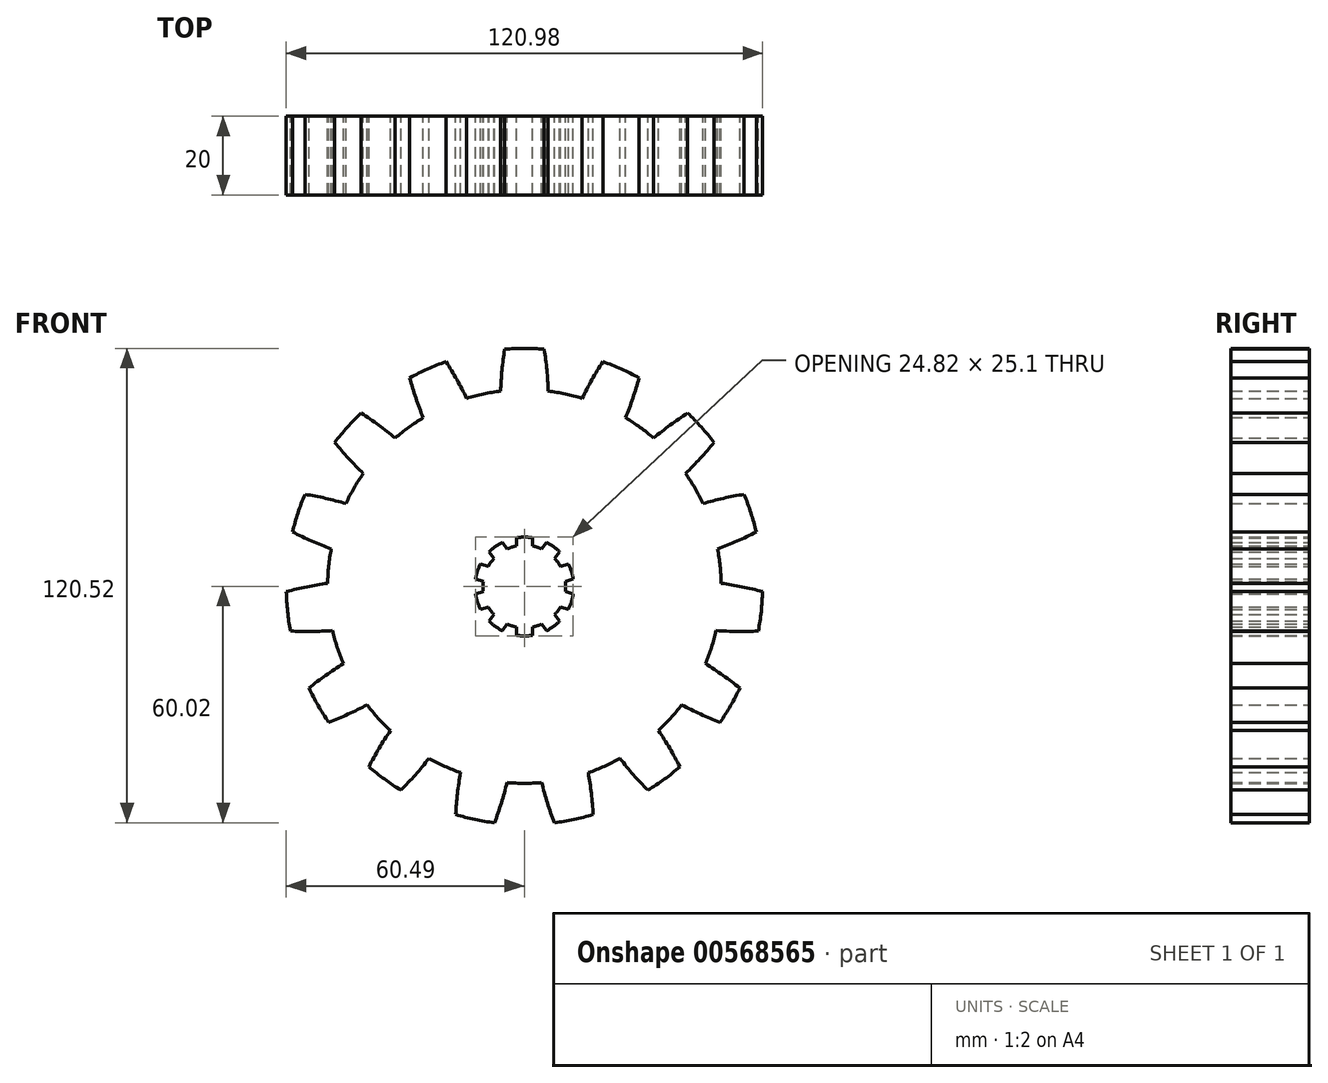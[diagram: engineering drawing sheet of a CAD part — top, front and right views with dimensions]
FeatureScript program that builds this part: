
annotation { "Feature Type Name" : "Feature", "Feature Type Description" : "" }
export const myFeature = defineFeature(function(context is Context, id is Id, definition is map)
    precondition{}
    {
        {
            var Q0;
            Q0=qCreatedBy(makeId("Front.planeOp"),FACE);
            var sketch = newSketch(context, id + "F0", { "sketchPlane" : qUnion([Q0])});
            skCircle(sketch, "E0", {"center": v(0, 0) * mm, "radius": 50 * mm});
            skLineSegment(sketch, "E1", {"start": v(-16.39, 46.5) * mm, "end": v(83.9, 46.5) * mm, "construction": true});
            skLineSegment(sketch, "E2", {"start": v(83.9, 46.5) * mm, "end": v(83.9, 27.65) * mm, "construction": true});
            skLineSegment(sketch, "E3", {"start": v(83.9, 46.5) * mm, "end": v(83.9, 51.66) * mm, "construction": true});
            skLineSegment(sketch, "E4", {"start": v(0, -2.7) * mm, "end": v(0, 89.14) * mm, "construction": true});
            skLineSegment(sketch, "E5", {"start": v(0, 50) * mm, "end": v(-34.34, 50) * mm, "construction": true});
            skArc(sketch, "E6", {"start": v(-5.04, 60.29) * mm, "mid": v(-5.7, 54.98) * mm, "end": v(-6.05, 49.63) * mm});
            skArc(sketch, "E7.MirrorCS", {"start": v(5.04, 60.29) * mm, "mid": v(5.7, 54.98) * mm, "end": v(6.05, 49.63) * mm});
            skArc(sketch, "E8.trimOffspring", {"start": v(5.04, 60.29) * mm, "mid": v(0, 60.5) * mm, "end": v(-5.04, 60.29) * mm});
            skArc(sketch, "E9.1.0", {"start": v(-19.92, 57.13) * mm, "mid": v(-24.6, 55.27) * mm, "end": v(-29.12, 53.03) * mm});
            skArc(sketch, "E9.2.0", {"start": v(-41.43, 44.09) * mm, "mid": v(-44.96, 40.48) * mm, "end": v(-48.17, 36.6) * mm});
            skArc(sketch, "E10.3.3.0", {"start": v(-55.78, 23.42) * mm, "mid": v(-57.54, 18.7) * mm, "end": v(-58.9, 13.84) * mm});
            skArc(sketch, "E10.3.4.0", {"start": v(-60.49, -1.3) * mm, "mid": v(-60.17, -6.32) * mm, "end": v(-59.43, -11.31) * mm});
            skArc(sketch, "E10.3.5.0", {"start": v(-54.73, -25.78) * mm, "mid": v(-52.4, -30.25) * mm, "end": v(-49.7, -34.5) * mm});
            skArc(sketch, "E10.3.6.0", {"start": v(-39.51, -45.81) * mm, "mid": v(-35.56, -48.95) * mm, "end": v(-31.36, -51.74) * mm});
            skArc(sketch, "E10.3.7.0", {"start": v(-17.46, -57.93) * mm, "mid": v(-12.58, -59.18) * mm, "end": v(-7.6, -60.02) * mm});
            skArc(sketch, "E10.3.8.0", {"start": v(7.6, -60.02) * mm, "mid": v(12.58, -59.18) * mm, "end": v(17.46, -57.93) * mm});
            skArc(sketch, "E10.3.9.0", {"start": v(31.36, -51.74) * mm, "mid": v(35.56, -48.95) * mm, "end": v(39.51, -45.81) * mm});
            skArc(sketch, "E10.3.10.0", {"start": v(49.7, -34.5) * mm, "mid": v(52.4, -30.25) * mm, "end": v(54.73, -25.78) * mm});
            skArc(sketch, "E10.3.11.0", {"start": v(59.43, -11.31) * mm, "mid": v(60.17, -6.32) * mm, "end": v(60.49, -1.3) * mm});
            skArc(sketch, "E10.3.12.0", {"start": v(58.9, 13.84) * mm, "mid": v(57.54, 18.7) * mm, "end": v(55.78, 23.42) * mm});
            skArc(sketch, "E10.3.13.0", {"start": v(48.17, 36.6) * mm, "mid": v(44.96, 40.48) * mm, "end": v(41.43, 44.09) * mm});
            skArc(sketch, "E10.3.14.0", {"start": v(29.12, 53.03) * mm, "mid": v(24.6, 55.27) * mm, "end": v(19.92, 57.13) * mm});
            skArc(sketch, "E11.1.0", {"start": v(-29.12, 53.03) * mm, "mid": v(-27.57, 47.9) * mm, "end": v(-25.71, 42.88) * mm});
            skArc(sketch, "E11.1.2", {"start": v(-19.92, 57.13) * mm, "mid": v(-17.15, 52.54) * mm, "end": v(-14.66, 47.8) * mm});
            skArc(sketch, "E11.2.0", {"start": v(-48.17, 36.6) * mm, "mid": v(-44.67, 32.55) * mm, "end": v(-40.93, 28.72) * mm});
            skArc(sketch, "E11.2.2", {"start": v(-41.43, 44.09) * mm, "mid": v(-37.04, 41.02) * mm, "end": v(-32.84, 37.7) * mm});
            skArc(sketch, "E11.3.0", {"start": v(-58.9, 13.84) * mm, "mid": v(-54.05, 11.57) * mm, "end": v(-49.07, 9.59) * mm});
            skArc(sketch, "E11.3.2", {"start": v(-55.78, 23.42) * mm, "mid": v(-50.52, 22.4) * mm, "end": v(-45.34, 21.09) * mm});
            skArc(sketch, "E11.4.0", {"start": v(-59.43, -11.31) * mm, "mid": v(-54.08, -11.42) * mm, "end": v(-48.73, -11.2) * mm});
            skArc(sketch, "E11.4.2", {"start": v(-60.49, -1.3) * mm, "mid": v(-55.27, -0.08) * mm, "end": v(-50, 0.82) * mm});
            skArc(sketch, "E11.5.0", {"start": v(-49.7, -34.5) * mm, "mid": v(-44.76, -32.42) * mm, "end": v(-39.96, -30.05) * mm});
            skArc(sketch, "E11.5.2", {"start": v(-54.73, -25.78) * mm, "mid": v(-50.46, -22.55) * mm, "end": v(-46, -19.58) * mm});
            skArc(sketch, "E11.6.0", {"start": v(-31.36, -51.74) * mm, "mid": v(-27.7, -47.83) * mm, "end": v(-24.28, -43.7) * mm});
            skArc(sketch, "E11.6.2", {"start": v(-39.51, -45.81) * mm, "mid": v(-36.93, -41.13) * mm, "end": v(-34.06, -36.6) * mm});
            skArc(sketch, "E11.7.0", {"start": v(-7.6, -60.02) * mm, "mid": v(-5.85, -54.96) * mm, "end": v(-4.4, -49.8) * mm});
            skArc(sketch, "E11.7.2", {"start": v(-17.46, -57.93) * mm, "mid": v(-17, -52.6) * mm, "end": v(-16.23, -47.3) * mm});
            skArc(sketch, "E11.8.0", {"start": v(17.46, -57.93) * mm, "mid": v(17, -52.6) * mm, "end": v(16.23, -47.3) * mm});
            skArc(sketch, "E11.8.2", {"start": v(7.6, -60.02) * mm, "mid": v(5.85, -54.96) * mm, "end": v(4.4, -49.8) * mm});
            skArc(sketch, "E11.9.0", {"start": v(39.51, -45.81) * mm, "mid": v(36.93, -41.13) * mm, "end": v(34.06, -36.6) * mm});
            skArc(sketch, "E11.9.2", {"start": v(31.36, -51.74) * mm, "mid": v(27.7, -47.83) * mm, "end": v(24.28, -43.7) * mm});
            skArc(sketch, "E11.10.0", {"start": v(54.73, -25.78) * mm, "mid": v(50.46, -22.55) * mm, "end": v(46, -19.58) * mm});
            skArc(sketch, "E11.10.2", {"start": v(49.7, -34.5) * mm, "mid": v(44.76, -32.42) * mm, "end": v(39.96, -30.05) * mm});
            skArc(sketch, "E11.11.0", {"start": v(60.49, -1.3) * mm, "mid": v(55.27, -0.08) * mm, "end": v(50, 0.82) * mm});
            skArc(sketch, "E11.11.2", {"start": v(59.43, -11.31) * mm, "mid": v(54.08, -11.42) * mm, "end": v(48.73, -11.2) * mm});
            skArc(sketch, "E11.12.0", {"start": v(55.78, 23.42) * mm, "mid": v(50.52, 22.4) * mm, "end": v(45.34, 21.09) * mm});
            skArc(sketch, "E11.12.2", {"start": v(58.9, 13.84) * mm, "mid": v(54.05, 11.57) * mm, "end": v(49.07, 9.59) * mm});
            skArc(sketch, "E11.13.0", {"start": v(41.43, 44.09) * mm, "mid": v(37.04, 41.02) * mm, "end": v(32.84, 37.7) * mm});
            skArc(sketch, "E11.13.2", {"start": v(48.17, 36.6) * mm, "mid": v(44.67, 32.55) * mm, "end": v(40.93, 28.72) * mm});
            skArc(sketch, "E11.14.0", {"start": v(19.92, 57.13) * mm, "mid": v(17.15, 52.54) * mm, "end": v(14.66, 47.8) * mm});
            skArc(sketch, "E11.14.2", {"start": v(29.12, 53.03) * mm, "mid": v(27.57, 47.9) * mm, "end": v(25.71, 42.88) * mm});
            skSolve(sketch);
        }
        {
            var Q0;
            {var subQ0=sQuery(id+"F0.wireOp",EDGE,"E0");var subQ18=makeQuery(id+"F0.imprint","INTERSECT",VERTEX,{"derivedFrom":[subQ0,sQuery(id+"F0.wireOp",EDGE,"E11.11.0")]});Q0=makeQuery(id+"F0.imprint","IMPRINT",FACE,{"disambiguationData":[TD([[makeQuery(id+"F0.imprint","IMPRINT",EDGE,{"disambiguationData":[TD([[subQ18,-1.0]])],"derivedFrom":subQ0}),1.0]])]});}
            var Q1;
            {var subQ0=sQuery(id+"F0.wireOp",EDGE,"E11.1.0");Q1=makeQuery(id+"F0.imprint","IMPRINT",FACE,{"disambiguationData":[TD([[makeQuery(id+"F0.imprint","IMPRINT",EDGE,{"derivedFrom":subQ0}),1.0]])]});}
            var Q2;
            {var subQ0=sQuery(id+"F0.wireOp",EDGE,"E6");Q2=makeQuery(id+"F0.imprint","IMPRINT",FACE,{"disambiguationData":[TD([[makeQuery(id+"F0.imprint","IMPRINT",EDGE,{"derivedFrom":subQ0}),1.0]])]});}
            var Q3;
            {var subQ0=sQuery(id+"F0.wireOp",EDGE,"E11.14.0");Q3=makeQuery(id+"F0.imprint","IMPRINT",FACE,{"disambiguationData":[TD([[makeQuery(id+"F0.imprint","IMPRINT",EDGE,{"derivedFrom":subQ0}),1.0]])]});}
            var Q4;
            {var subQ0=sQuery(id+"F0.wireOp",EDGE,"E11.13.0");Q4=makeQuery(id+"F0.imprint","IMPRINT",FACE,{"disambiguationData":[TD([[makeQuery(id+"F0.imprint","IMPRINT",EDGE,{"derivedFrom":subQ0}),1.0]])]});}
            var Q5;
            {var subQ0=sQuery(id+"F0.wireOp",EDGE,"E11.12.0");Q5=makeQuery(id+"F0.imprint","IMPRINT",FACE,{"disambiguationData":[TD([[makeQuery(id+"F0.imprint","IMPRINT",EDGE,{"derivedFrom":subQ0}),1.0]])]});}
            var Q6;
            {var subQ0=sQuery(id+"F0.wireOp",EDGE,"E11.11.0");Q6=makeQuery(id+"F0.imprint","IMPRINT",FACE,{"disambiguationData":[TD([[makeQuery(id+"F0.imprint","IMPRINT",EDGE,{"derivedFrom":subQ0}),1.0]])]});}
            var Q7;
            {var subQ0=sQuery(id+"F0.wireOp",EDGE,"E11.10.0");Q7=makeQuery(id+"F0.imprint","IMPRINT",FACE,{"disambiguationData":[TD([[makeQuery(id+"F0.imprint","IMPRINT",EDGE,{"derivedFrom":subQ0}),1.0]])]});}
            var Q8;
            {var subQ0=sQuery(id+"F0.wireOp",EDGE,"E11.9.0");Q8=makeQuery(id+"F0.imprint","IMPRINT",FACE,{"disambiguationData":[TD([[makeQuery(id+"F0.imprint","IMPRINT",EDGE,{"derivedFrom":subQ0}),1.0]])]});}
            var Q9;
            {var subQ0=sQuery(id+"F0.wireOp",EDGE,"E11.8.0");Q9=makeQuery(id+"F0.imprint","IMPRINT",FACE,{"disambiguationData":[TD([[makeQuery(id+"F0.imprint","IMPRINT",EDGE,{"derivedFrom":subQ0}),1.0]])]});}
            var Q10;
            {var subQ0=sQuery(id+"F0.wireOp",EDGE,"E11.7.0");Q10=makeQuery(id+"F0.imprint","IMPRINT",FACE,{"disambiguationData":[TD([[makeQuery(id+"F0.imprint","IMPRINT",EDGE,{"derivedFrom":subQ0}),1.0]])]});}
            var Q11;
            {var subQ0=sQuery(id+"F0.wireOp",EDGE,"E11.6.0");Q11=makeQuery(id+"F0.imprint","IMPRINT",FACE,{"disambiguationData":[TD([[makeQuery(id+"F0.imprint","IMPRINT",EDGE,{"derivedFrom":subQ0}),1.0]])]});}
            var Q12;
            {var subQ0=sQuery(id+"F0.wireOp",EDGE,"E11.5.0");Q12=makeQuery(id+"F0.imprint","IMPRINT",FACE,{"disambiguationData":[TD([[makeQuery(id+"F0.imprint","IMPRINT",EDGE,{"derivedFrom":subQ0}),1.0]])]});}
            var Q13;
            {var subQ0=sQuery(id+"F0.wireOp",EDGE,"E11.4.0");Q13=makeQuery(id+"F0.imprint","IMPRINT",FACE,{"disambiguationData":[TD([[makeQuery(id+"F0.imprint","IMPRINT",EDGE,{"derivedFrom":subQ0}),1.0]])]});}
            var Q14;
            {var subQ0=sQuery(id+"F0.wireOp",EDGE,"E11.3.0");Q14=makeQuery(id+"F0.imprint","IMPRINT",FACE,{"disambiguationData":[TD([[makeQuery(id+"F0.imprint","IMPRINT",EDGE,{"derivedFrom":subQ0}),1.0]])]});}
            var Q15;
            {var subQ0=sQuery(id+"F0.wireOp",EDGE,"E11.2.0");Q15=makeQuery(id+"F0.imprint","IMPRINT",FACE,{"disambiguationData":[TD([[makeQuery(id+"F0.imprint","IMPRINT",EDGE,{"derivedFrom":subQ0}),1.0]])]});}
            extrude(context, id + "F1", {"entities" : qUnion([Q0, Q1, Q2, Q3, Q4, Q5, Q6, Q7, Q8, Q9, Q10, Q11, Q12, Q13, Q14, Q15]), "depth" : 20 * mm, "offsetDistance" : 25 * mm});
        }
        {
            var Q0;
            Q0=qCreatedBy(makeId("Front.planeOp"),FACE);
            var sketch = newSketch(context, id + "F2", { "sketchPlane" : qUnion([Q0])});
            skCircle(sketch, "E12", {"center": v(0, 0) * mm, "radius": 10.5 * mm});
            skArc(sketch, "E13", {"start": v(2.05, 12.38) * mm, "mid": v(0, 12.55) * mm, "end": v(-2.05, 12.38) * mm});
            skLineSegment(sketch, "E14", {"start": v(-2.05, 10.3) * mm, "end": v(-2.05, 12.38) * mm});
            skLineSegment(sketch, "E15", {"start": v(2.05, 10.3) * mm, "end": v(2.05, 12.38) * mm});
            skPoint(sketch, "E16.end.orphan", {"position": v(2.05, 0) * mm});
            skLineSegment(sketch, "E17.1.0", {"start": v(-7.71, 7.13) * mm, "end": v(-8.94, 8.81) * mm});
            skArc(sketch, "E17.1.1", {"start": v(-5.62, 11.22) * mm, "mid": v(-7.38, 10.15) * mm, "end": v(-8.94, 8.81) * mm});
            skLineSegment(sketch, "E17.1.2", {"start": v(-4.4, 9.54) * mm, "end": v(-5.62, 11.22) * mm});
            skLineSegment(sketch, "E17.2.0", {"start": v(-10.43, 1.23) * mm, "end": v(-12.4, 1.88) * mm});
            skArc(sketch, "E17.2.1", {"start": v(-11.14, 5.78) * mm, "mid": v(-11.94, 3.88) * mm, "end": v(-12.4, 1.88) * mm});
            skLineSegment(sketch, "E17.2.2", {"start": v(-9.16, 5.13) * mm, "end": v(-11.14, 5.78) * mm});
            skLineSegment(sketch, "E17.3.0", {"start": v(-9.16, -5.13) * mm, "end": v(-11.14, -5.78) * mm});
            skArc(sketch, "E17.3.1", {"start": v(-12.4, -1.88) * mm, "mid": v(-11.94, -3.88) * mm, "end": v(-11.14, -5.78) * mm});
            skLineSegment(sketch, "E17.3.2", {"start": v(-10.43, -1.23) * mm, "end": v(-12.4, -1.88) * mm});
            skLineSegment(sketch, "E17.4.0", {"start": v(-4.4, -9.54) * mm, "end": v(-5.62, -11.22) * mm});
            skArc(sketch, "E17.4.1", {"start": v(-8.94, -8.81) * mm, "mid": v(-7.38, -10.15) * mm, "end": v(-5.62, -11.22) * mm});
            skLineSegment(sketch, "E17.4.2", {"start": v(-7.71, -7.13) * mm, "end": v(-8.94, -8.81) * mm});
            skLineSegment(sketch, "E17.5.0", {"start": v(2.05, -10.3) * mm, "end": v(2.05, -12.38) * mm});
            skArc(sketch, "E17.5.1", {"start": v(-2.05, -12.38) * mm, "mid": v(0, -12.55) * mm, "end": v(2.05, -12.38) * mm});
            skLineSegment(sketch, "E17.5.2", {"start": v(-2.05, -10.3) * mm, "end": v(-2.05, -12.38) * mm});
            skLineSegment(sketch, "E17.6.0", {"start": v(7.71, -7.13) * mm, "end": v(8.94, -8.81) * mm});
            skArc(sketch, "E17.6.1", {"start": v(5.62, -11.22) * mm, "mid": v(7.38, -10.15) * mm, "end": v(8.94, -8.81) * mm});
            skLineSegment(sketch, "E17.6.2", {"start": v(4.4, -9.54) * mm, "end": v(5.62, -11.22) * mm});
            skLineSegment(sketch, "E17.7.0", {"start": v(10.43, -1.23) * mm, "end": v(12.4, -1.88) * mm});
            skArc(sketch, "E17.7.1", {"start": v(11.14, -5.78) * mm, "mid": v(11.94, -3.88) * mm, "end": v(12.4, -1.88) * mm});
            skLineSegment(sketch, "E17.7.2", {"start": v(9.16, -5.13) * mm, "end": v(11.14, -5.78) * mm});
            skLineSegment(sketch, "E17.8.0", {"start": v(9.16, 5.13) * mm, "end": v(11.14, 5.78) * mm});
            skArc(sketch, "E17.8.1", {"start": v(12.4, 1.88) * mm, "mid": v(11.94, 3.88) * mm, "end": v(11.14, 5.78) * mm});
            skLineSegment(sketch, "E17.8.2", {"start": v(10.43, 1.23) * mm, "end": v(12.4, 1.88) * mm});
            skLineSegment(sketch, "E17.9.0", {"start": v(4.4, 9.54) * mm, "end": v(5.62, 11.22) * mm});
            skArc(sketch, "E17.9.1", {"start": v(8.94, 8.81) * mm, "mid": v(7.38, 10.15) * mm, "end": v(5.62, 11.22) * mm});
            skLineSegment(sketch, "E17.9.2", {"start": v(7.71, 7.13) * mm, "end": v(8.94, 8.81) * mm});
            skSolve(sketch);
        }
        {
            var Q0;
            {var subQ0=sQuery(id+"F2.wireOp",EDGE,"E12");var subQ8=makeQuery(id+"F2.imprint","INTERSECT",VERTEX,{"derivedFrom":[subQ0,sQuery(id+"F2.wireOp",EDGE,"E17.8.0")]});Q0=makeQuery(id+"F2.imprint","IMPRINT",FACE,{"disambiguationData":[TD([[makeQuery(id+"F2.imprint","IMPRINT",EDGE,{"disambiguationData":[TD([[subQ8,1.0]])],"derivedFrom":subQ0}),1.0]])]});}
            var Q1;
            {var subQ0=sQuery(id+"F2.wireOp",EDGE,"E17.1.0");Q1=makeQuery(id+"F2.imprint","IMPRINT",FACE,{"disambiguationData":[TD([[makeQuery(id+"F2.imprint","IMPRINT",EDGE,{"derivedFrom":subQ0}),-1.0]])]});}
            var Q2;
            {var subQ0=sQuery(id+"F2.wireOp",EDGE,"E17.2.0");Q2=makeQuery(id+"F2.imprint","IMPRINT",FACE,{"disambiguationData":[TD([[makeQuery(id+"F2.imprint","IMPRINT",EDGE,{"derivedFrom":subQ0}),-1.0]])]});}
            var Q3;
            Q3=makeQuery(id+"F2.imprint","IMPRINT",FACE,{"disambiguationData":[TD([[makeQuery(id+"F2.imprint","IMPRINT",EDGE,{"derivedFrom":sQuery(id+"F2.wireOp",EDGE,"E13")}),1.0]])]});
            var Q4;
            {var subQ0=sQuery(id+"F2.wireOp",EDGE,"E17.9.0");Q4=makeQuery(id+"F2.imprint","IMPRINT",FACE,{"disambiguationData":[TD([[makeQuery(id+"F2.imprint","IMPRINT",EDGE,{"derivedFrom":subQ0}),-1.0]])]});}
            var Q5;
            {var subQ0=sQuery(id+"F2.wireOp",EDGE,"E17.8.0");Q5=makeQuery(id+"F2.imprint","IMPRINT",FACE,{"disambiguationData":[TD([[makeQuery(id+"F2.imprint","IMPRINT",EDGE,{"derivedFrom":subQ0}),-1.0]])]});}
            var Q6;
            {var subQ0=sQuery(id+"F2.wireOp",EDGE,"E17.7.0");Q6=makeQuery(id+"F2.imprint","IMPRINT",FACE,{"disambiguationData":[TD([[makeQuery(id+"F2.imprint","IMPRINT",EDGE,{"derivedFrom":subQ0}),-1.0]])]});}
            var Q7;
            {var subQ0=sQuery(id+"F2.wireOp",EDGE,"E17.6.0");Q7=makeQuery(id+"F2.imprint","IMPRINT",FACE,{"disambiguationData":[TD([[makeQuery(id+"F2.imprint","IMPRINT",EDGE,{"derivedFrom":subQ0}),-1.0]])]});}
            var Q8;
            {var subQ0=sQuery(id+"F2.wireOp",EDGE,"E17.5.0");Q8=makeQuery(id+"F2.imprint","IMPRINT",FACE,{"disambiguationData":[TD([[makeQuery(id+"F2.imprint","IMPRINT",EDGE,{"derivedFrom":subQ0}),-1.0]])]});}
            var Q9;
            {var subQ0=sQuery(id+"F2.wireOp",EDGE,"E17.4.0");Q9=makeQuery(id+"F2.imprint","IMPRINT",FACE,{"disambiguationData":[TD([[makeQuery(id+"F2.imprint","IMPRINT",EDGE,{"derivedFrom":subQ0}),-1.0]])]});}
            var Q10;
            {var subQ0=sQuery(id+"F2.wireOp",EDGE,"E17.3.0");Q10=makeQuery(id+"F2.imprint","IMPRINT",FACE,{"disambiguationData":[TD([[makeQuery(id+"F2.imprint","IMPRINT",EDGE,{"derivedFrom":subQ0}),-1.0]])]});}
            extrude(context, id + "F3", {"entities" : qUnion([Q0, Q1, Q2, Q3, Q4, Q5, Q6, Q7, Q8, Q9, Q10]), "operationType" : NewBodyOperationType.REMOVE, "depth" : 20 * mm, "offsetDistance" : 25 * mm});
        }
    });
